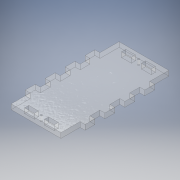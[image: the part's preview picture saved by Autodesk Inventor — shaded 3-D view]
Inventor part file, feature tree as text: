
AUTODESK INVENTOR PART (.ipt)
format: ipt  version: 2019 (Build 230136000, 136)  size: 182,272 bytes
history: native  units: mm
features: extrude x1, sketch x1
ambient origin geometry x8: Origin, YZ Plane, XZ Plane, XY Plane, X Axis, Y Axis, Z Axis, Center Point
bodies: Solid1 (feature_tree)
feature tree (2):
  extrude  "Extrusion1"  Depth=130.0mm
  sketch  "Sketch1"  dims[d0=60.0mm d1=130.0mm d2=6.0mm d3=12.0mm d4=12.0mm d5=12.0mm d6=6.0mm d9=4.0mm d10=5.1mm d11=6.0mm d12=0.0mm d13=12.3mm d14=11.7mm d15=2.25mm d16=2.25mm d17=6.15mm d18=2.55mm d19=6.3mm d20=2.55mm]
